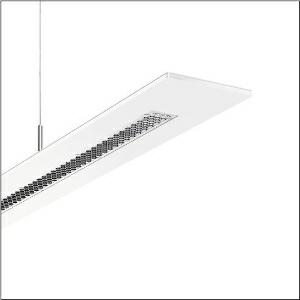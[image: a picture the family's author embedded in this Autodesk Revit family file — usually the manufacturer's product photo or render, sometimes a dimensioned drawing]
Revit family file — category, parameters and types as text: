
# Revit family: arktika_r__21_5mb2512l30830_74ae
name_source: partatom
category: Lighting Fixtures
units: mm (PartAtom-declared; Revit-internal decimal feet)

## family parameters
Cut with Voids When Loaded = No
Host = Face
Light Source = No
Part Type = Normal
Room Calculation Point = No
Round Connector Dimension = Use Diameter
Shared = No

## types (1)
- Arktika® 21 (1 x LED 3000K / CRI = 80 (unbekannt), 3670 lm, 3000K)
    Apparent Load = 31 VA
    CIE Flux Codes = 81 100 100 79 100
    Color Rendering = 80
    Color Temperature = 3000K
    Default Elevation = 1800 mm
    Description = Arktika® 21, office luminaire, primary anti-glare with honeycomb louvre, of plastic, aluminium vaporised, highly specular, light emission: direct/indirect distribution, primary light characteristic: symmetric, installation type: suspended mounting, LED rated luminous flux: 3.670 lm, light colour: 830, colour temperature: 3000K, control gear: ECG, with terminal, 3-pole, mains connection: 220..240V, AC, 50/60Hz, rated input power: 31W, housing, of aluminium, powder-coated, traffic white (RAL 9016), 1-length, length: 1.250 mm, width: 120 mm, height: 8mm, protection rating (complete): IP20, insulation class (complete): insulation class II (safety insulation), certification: CE, packaging unit: 1 piece
    Height = 8 mm  [stored 0.0262467 ft]
    Lamp = 1 x LED 3000K / CRI >= 80 (unbekannt)
    Lamp Light Flux = 3670 lm
    Lamp count = 1
    Length = 1250 mm
    Luminous efficacy = 120 lm/W
    Manufacturer = Siteco
    ModVariant = No
    Model = 5MB2512L30830
    Mounting Place = Ceiling
    Mounting Type = Pendant
    Number of Poles = 1
    OnlyDefault = Yes
    Power Factor = 1
    Product Name = Arktika® 21
    Product group = office luminaire | ceiling pendant
    ProductGroupID = 905
    Protection Class = Protection class II
    Protection Degree = IP 20
    RLX_Detail_Level = 1
    RlxData = <blob elided: 36041 chars, md5=9e37de7e>
    Socket = socket
    Standby Power = 0 W
    System Light Flux = 3670 lm
    System Power = 31 W
    Type Comments = Product without accessories
    Type Image = l_1006128.jpg
    URL = http://relux.com
    VarID = ---
    Voltage = 0 V
    Weight = 0.00 kg
    Width = 120 mm

note: [stored X ft] marks values corroborated as IEEE doubles in the binary element streams (Revit-internal decimal feet)

## geometry (parser evidence)
native form markers: Blend x4, Sweep x13
no freeform markers — native parametric forms only
